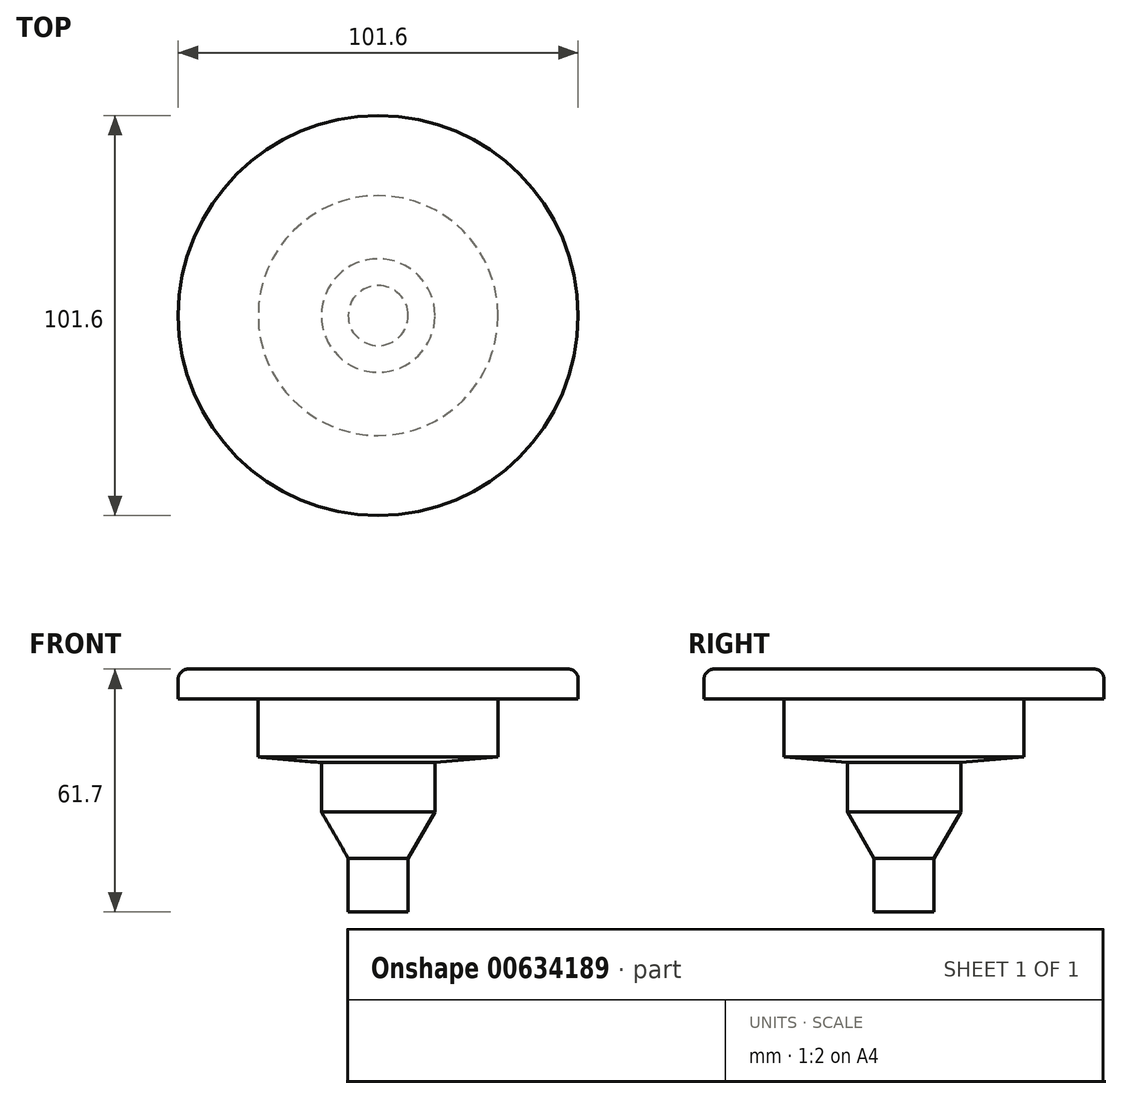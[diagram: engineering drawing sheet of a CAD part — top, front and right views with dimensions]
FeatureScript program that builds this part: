
annotation { "Feature Type Name" : "Feature", "Feature Type Description" : "" }
export const myFeature = defineFeature(function(context is Context, id is Id, definition is map)
    precondition{}
    {
        {
            var Q0;
            Q0=qCreatedBy(makeId("Front.planeOp"),FACE);
            var sketch = newSketch(context, id + "F0", { "sketchPlane" : qUnion([Q0])});
            skLineSegment(sketch, "E0", {"start": v(0, 0) * mm, "end": v(0, 61.7) * mm});
            skLineSegment(sketch, "E1", {"start": v(0, 61.7) * mm, "end": v(50.8, 61.7) * mm});
            skLineSegment(sketch, "E2", {"start": v(50.8, 61.7) * mm, "end": v(50.8, 54.08) * mm});
            skLineSegment(sketch, "E3", {"start": v(50.8, 54.08) * mm, "end": v(30.48, 54.08) * mm});
            skLineSegment(sketch, "E4", {"start": v(30.48, 54.08) * mm, "end": v(30.48, 39.32) * mm});
            skLineSegment(sketch, "E5", {"start": v(30.48, 39.32) * mm, "end": v(14.43, 37.92) * mm});
            skLineSegment(sketch, "E6", {"start": v(14.43, 37.92) * mm, "end": v(14.43, 25.42) * mm});
            skLineSegment(sketch, "E7", {"start": v(14.43, 25.42) * mm, "end": v(7.62, 13.63) * mm});
            skLineSegment(sketch, "E8", {"start": v(7.62, 13.63) * mm, "end": v(7.62, 0) * mm});
            skLineSegment(sketch, "E9", {"start": v(7.62, 0) * mm, "end": v(0, 0) * mm});
            skSolve(sketch);
        }
        {
            var Q0;
            Q0=makeQuery(id+"F0.imprint","IMPRINT",FACE,{"disambiguationData":[TD([[makeQuery(id+"F0.imprint","IMPRINT",EDGE,{"derivedFrom":sQuery(id+"F0.wireOp",EDGE,"E0")}),-1.0]])]});
            var Q1;
            Q1=sQuery(id+"F0.wireOp",EDGE,"E0");
            revolve(context, id + "F1", {"entities" : qUnion([Q0]), "axis" : qUnion([Q1]), "revolveType" : RevolveType.FULL});
        }
        {
            var Q0;
            Q0=makeQuery(id+"F1.opRevolve","SWEPT_FACE",FACE,{"disambiguationData":[OSD([sQuery(id+"F0.wireOp",EDGE,"E1")])]});
            fillet(context, id + "F2", {"entities" : qUnion([Q0]), "radius" : 2.54 * mm, "tangentPropagation" : true, "allowEdgeOverflow" : false});
        }
    });
